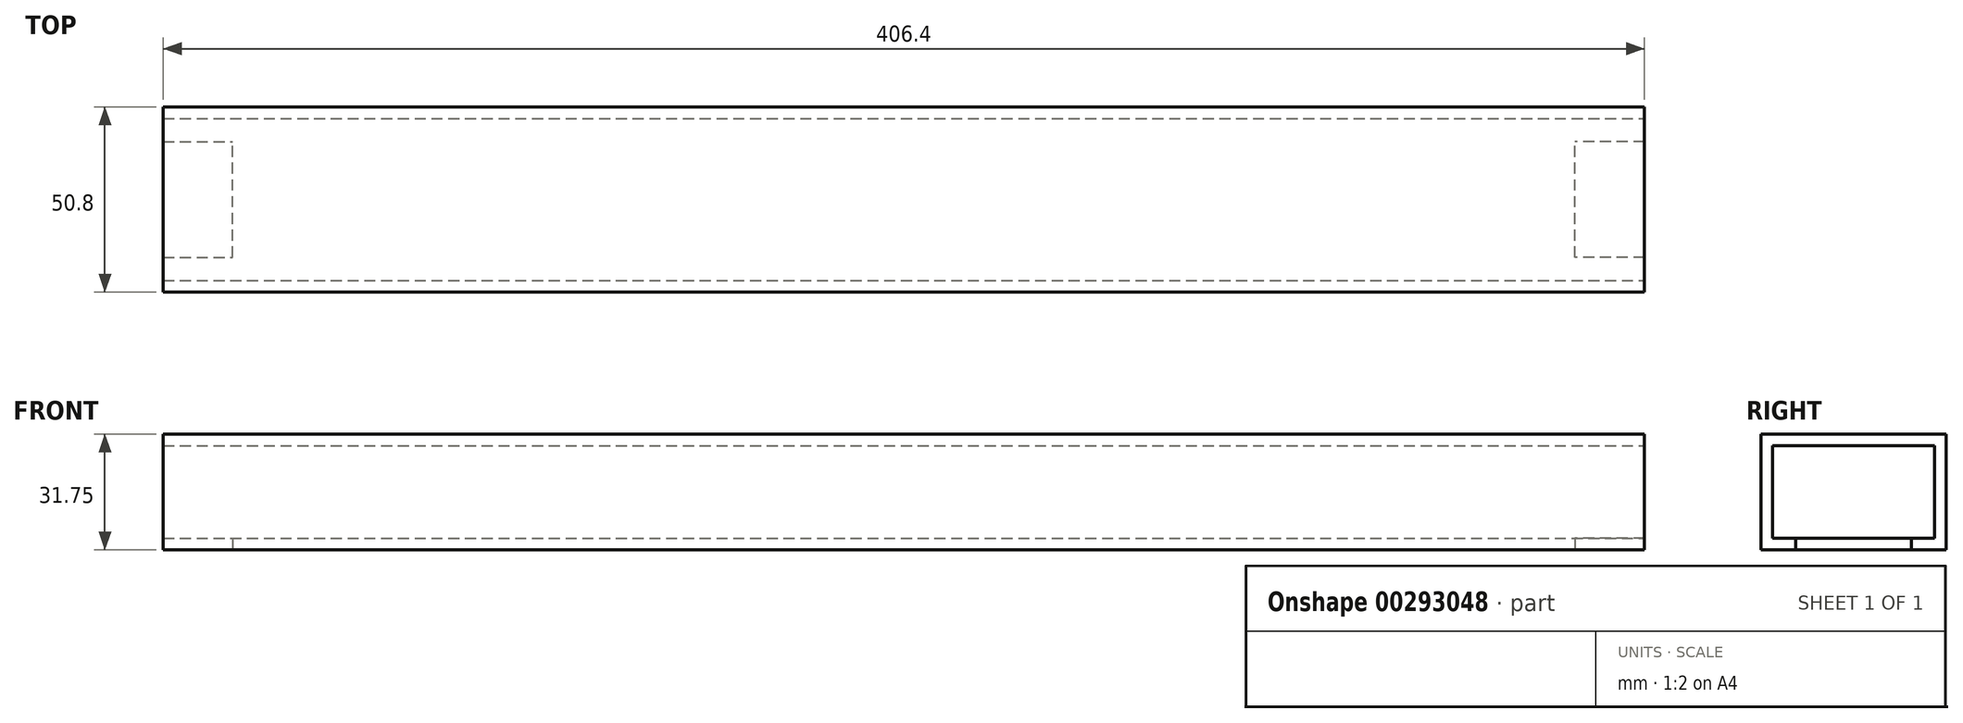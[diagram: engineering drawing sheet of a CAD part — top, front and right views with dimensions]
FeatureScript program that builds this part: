
annotation { "Feature Type Name" : "Feature", "Feature Type Description" : "" }
export const myFeature = defineFeature(function(context is Context, id is Id, definition is map)
    precondition{}
    {
        {
            var Q0;
            Q0=qCreatedBy(makeId("Front.planeOp"),FACE);
            var sketch = newSketch(context, id + "F0", { "sketchPlane" : qUnion([Q0])});
            skLineSegment(sketch, "E0.bottom", {"start": v(0, 0) * mm, "end": v(406.4, 0) * mm});
            skLineSegment(sketch, "E0.top", {"start": v(0, 31.75) * mm, "end": v(406.4, 31.75) * mm});
            skLineSegment(sketch, "E0.left", {"start": v(0, 0) * mm, "end": v(0, 31.75) * mm});
            skLineSegment(sketch, "E0.right", {"start": v(406.4, 0) * mm, "end": v(406.4, 31.75) * mm});
            skSolve(sketch);
        }
        {
            var Q0;
            Q0=makeQuery(id+"F0.imprint","IMPRINT",FACE,{"disambiguationData":[TD([[makeQuery(id+"F0.imprint","IMPRINT",EDGE,{"derivedFrom":sQuery(id+"F0.wireOp",EDGE,"E0.bottom")}),1.0]])]});
            extrude(context, id + "F1", {"entities" : qUnion([Q0]), "depth" : 50.8 * mm});
        }
        {
            var Q0;
            Q0=makeQuery(id+"F1.opExtrude","SWEPT_FACE",FACE,{"disambiguationData":[OSD([sQuery(id+"F0.wireOp",EDGE,"E0.left")])]});
            var Q1;
            Q1=makeQuery(id+"F1.opExtrude","SWEPT_FACE",FACE,{"disambiguationData":[OSD([sQuery(id+"F0.wireOp",EDGE,"E0.right")])]});
            shell(context, id + "F2", {"entities" : qUnion([Q0, Q1]), "thickness" : 3.17 * mm});
        }
        {
            var Q0;
            Q0=makeQuery(id+"F1.opExtrude","SWEPT_FACE",FACE,{"disambiguationData":[OSD([sQuery(id+"F0.wireOp",EDGE,"E0.bottom")])]});
            var sketch = newSketch(context, id + "F3", { "sketchPlane" : qUnion([Q0])});
            skLineSegment(sketch, "E1.0.0", {"start": v(0, 0) * mm, "end": v(406.4, 0) * mm});
            skLineSegment(sketch, "E1.0.1", {"start": v(406.4, 0) * mm, "end": v(406.4, 50.8) * mm});
            skLineSegment(sketch, "E1.0.2", {"start": v(406.4, 50.8) * mm, "end": v(0, 50.8) * mm});
            skLineSegment(sketch, "E1.0.3", {"start": v(0, 50.8) * mm, "end": v(0, 0) * mm});
            skLineSegment(sketch, "E2.bottom", {"start": v(0, 41.28) * mm, "end": v(19.05, 41.28) * mm});
            skLineSegment(sketch, "E2.top", {"start": v(0, 9.53) * mm, "end": v(19.05, 9.53) * mm});
            skLineSegment(sketch, "E2.left", {"start": v(0, 41.28) * mm, "end": v(0, 9.53) * mm});
            skLineSegment(sketch, "E2.right", {"start": v(19.05, 41.28) * mm, "end": v(19.05, 9.53) * mm});
            skLineSegment(sketch, "E3", {"start": v(203.2, 0) * mm, "end": v(203.2, 50.8) * mm, "construction": true});
            skPoint(sketch, "E4", {"position": v(19.05, 25.4) * mm});
            skPoint(sketch, "E5", {"position": v(203.2, 25.4) * mm});
            skLineSegment(sketch, "E6.MirrorCS", {"start": v(406.4, 9.53) * mm, "end": v(387.35, 9.53) * mm});
            skLineSegment(sketch, "E7.MirrorCS", {"start": v(387.35, 41.28) * mm, "end": v(387.35, 9.53) * mm});
            skLineSegment(sketch, "E8.MirrorCS", {"start": v(406.4, 41.28) * mm, "end": v(387.35, 41.28) * mm});
            skSolve(sketch);
        }
        {
            var Q0;
            Q0=makeQuery(id+"F3.imprint","IMPRINT",FACE,{"disambiguationData":[TD([[makeQuery(id+"F3.imprint","IMPRINT",EDGE,{"derivedFrom":sQuery(id+"F3.wireOp",EDGE,"E2.bottom")}),-1.0]])]});
            var Q1;
            {var subQ0=sQuery(id+"F3.wireOp",EDGE,"E6.MirrorCS");Q1=makeQuery(id+"F3.imprint","IMPRINT",FACE,{"disambiguationData":[TD([[makeQuery(id+"F3.imprint","IMPRINT",EDGE,{"derivedFrom":subQ0}),-1.0]])]});}
            extrude(context, id + "F4", {"entities" : qUnion([Q0, Q1]), "operationType" : NewBodyOperationType.REMOVE, "oppositeDirection" : true, "depth" : 3.17 * mm});
        }
    });
